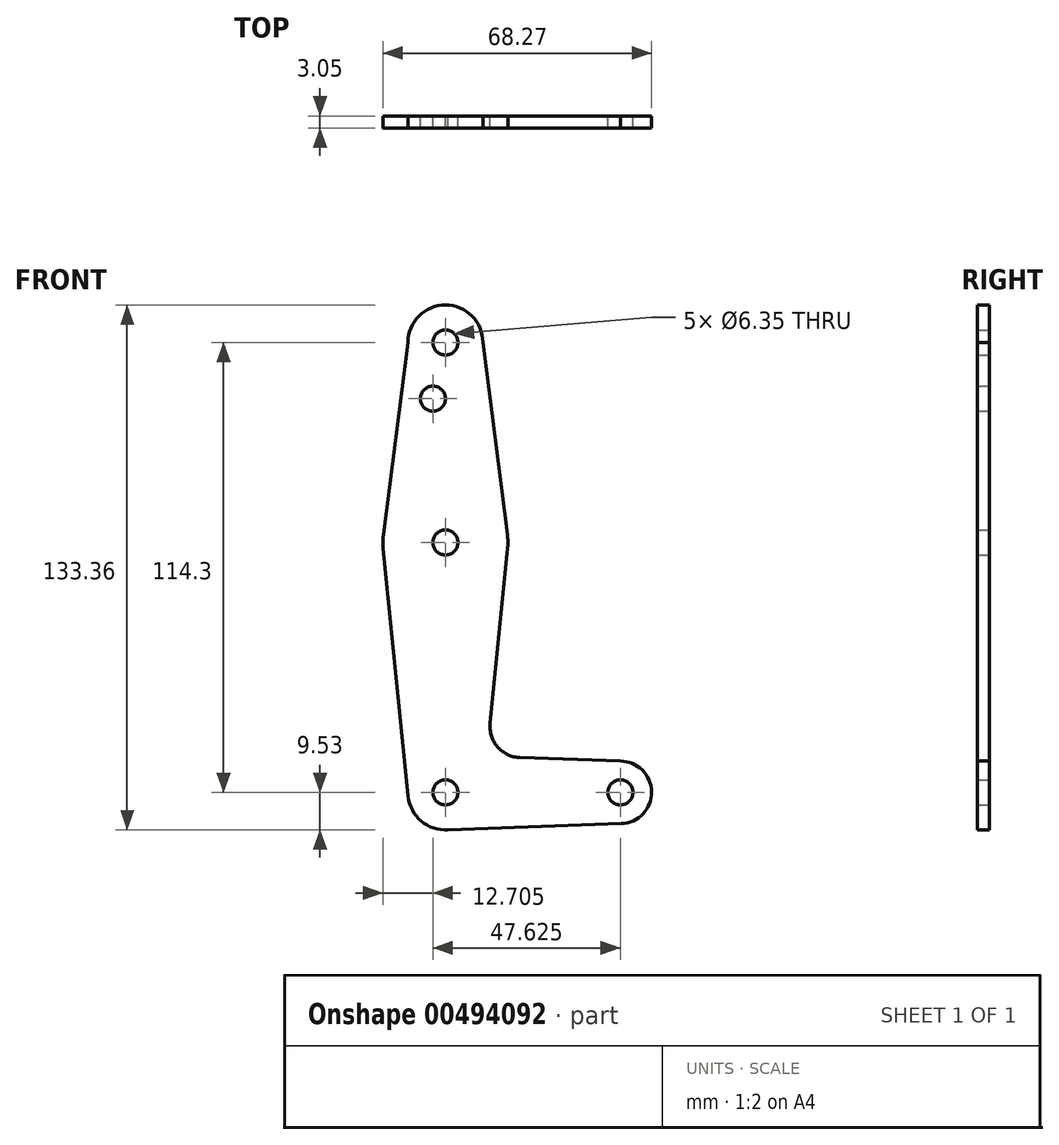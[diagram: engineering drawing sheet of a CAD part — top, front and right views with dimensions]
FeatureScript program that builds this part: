
annotation { "Feature Type Name" : "Feature", "Feature Type Description" : "" }
export const myFeature = defineFeature(function(context is Context, id is Id, definition is map)
    precondition{}
    {
        {
            var Q0;
            Q0=qCreatedBy(makeId("Front.planeOp"),FACE);
            var sketch = newSketch(context, id + "F0", { "sketchPlane" : qUnion([Q0])});
            skLineSegment(sketch, "E0", {"start": v(0, 114.3) * mm, "end": v(0, 0) * mm, "construction": true});
            skLineSegment(sketch, "E1", {"start": v(0, 0) * mm, "end": v(44.45, 0) * mm, "construction": true});
            skCircle(sketch, "E2", {"center": v(0, 114.3) * mm, "radius": 9.53 * mm});
            skCircle(sketch, "E3", {"center": v(0, 0) * mm, "radius": 9.53 * mm});
            skCircle(sketch, "E4", {"center": v(44.45, 0) * mm, "radius": 7.94 * mm});
            skCircle(sketch, "E5", {"center": v(0, 63.5) * mm, "radius": 15.88 * mm});
            skLineSegment(sketch, "E6", {"start": v(9.53, 114.3) * mm, "end": v(15.75, 65.5) * mm});
            skLineSegment(sketch, "E7", {"start": v(-9.52, 114.3) * mm, "end": v(-15.75, 65.5) * mm});
            skLineSegment(sketch, "E8", {"start": v(18.97, 8.85) * mm, "end": v(44.45, 7.94) * mm});
            skLineSegment(sketch, "E9", {"start": v(0, -9.53) * mm, "end": v(44.73, -7.93) * mm});
            skLineSegment(sketch, "E10", {"start": v(15.8, 61.91) * mm, "end": v(11.34, 17.59) * mm});
            skLineSegment(sketch, "E11", {"start": v(-15.8, 61.91) * mm, "end": v(-9.48, -0.95) * mm});
            skCircle(sketch, "E12", {"center": v(0, 114.3) * mm, "radius": 3.18 * mm});
            skCircle(sketch, "E13", {"center": v(0, 63.5) * mm, "radius": 3.18 * mm});
            skCircle(sketch, "E14", {"center": v(0, 0) * mm, "radius": 3.18 * mm});
            skCircle(sketch, "E15", {"center": v(44.45, 0) * mm, "radius": 3.18 * mm});
            skCircle(sketch, "E16", {"center": v(-3.17, 100.03) * mm, "radius": 3.18 * mm});
            skArc(sketch, "E17.filletArc", {"start": v(11.34, 17.59) * mm, "mid": v(13.26, 11.57) * mm, "end": v(18.97, 8.85) * mm});
            skSolve(sketch);
        }
        {
            var Q0;
            Q0 = qSketchRegion(id + "F0", true);
            extrude(context, id + "F1", {"entities" : qUnion([Q0]), "depth" : 3.05 * mm});
        }
    });
